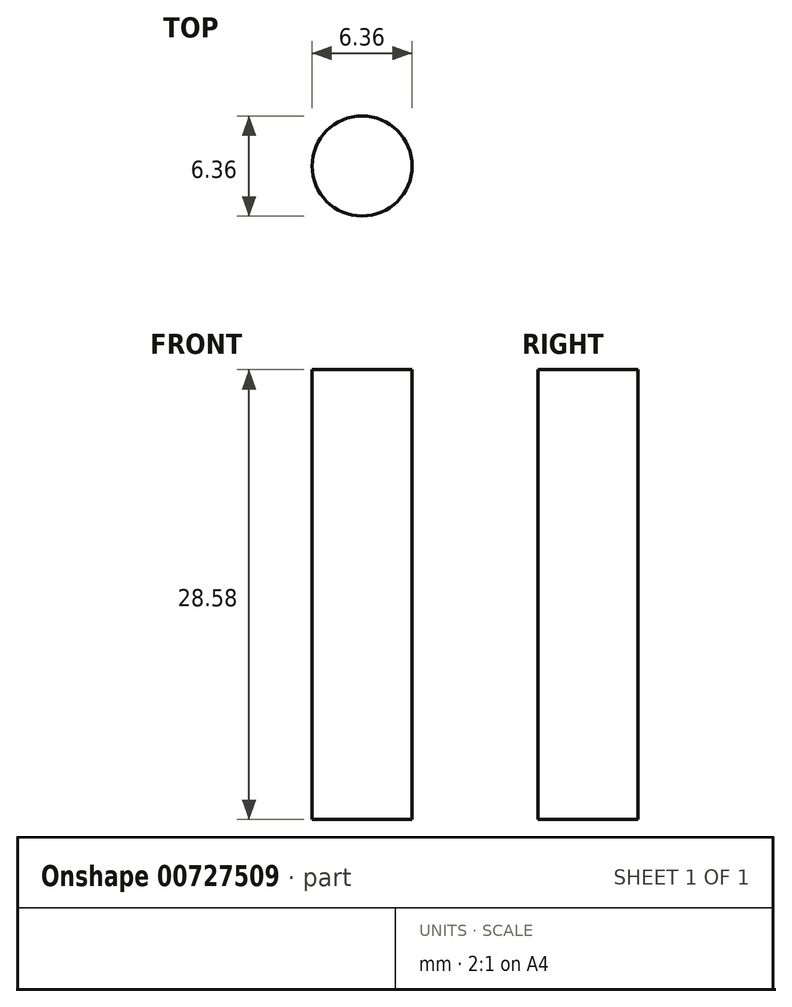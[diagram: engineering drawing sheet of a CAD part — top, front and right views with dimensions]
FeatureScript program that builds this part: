
annotation { "Feature Type Name" : "Feature", "Feature Type Description" : "" }
export const myFeature = defineFeature(function(context is Context, id is Id, definition is map)
    precondition{}
    {
        {
            var Q0;
            Q0=qCreatedBy(makeId("Top.planeOp"),FACE);
            var sketch = newSketch(context, id + "F0", { "sketchPlane" : qUnion([Q0])});
            skCircle(sketch, "E0", {"center": v(0, 0) * mm, "radius": 3.18 * mm});
            skSolve(sketch);
        }
        {
            var Q0;
            Q0 = qSketchRegion(id + "F0", true);
            extrude(context, id + "F1", {"entities" : qUnion([Q0]), "depth" : 28.57 * mm, "offsetDistance" : 25.4 * mm});
        }
    });
